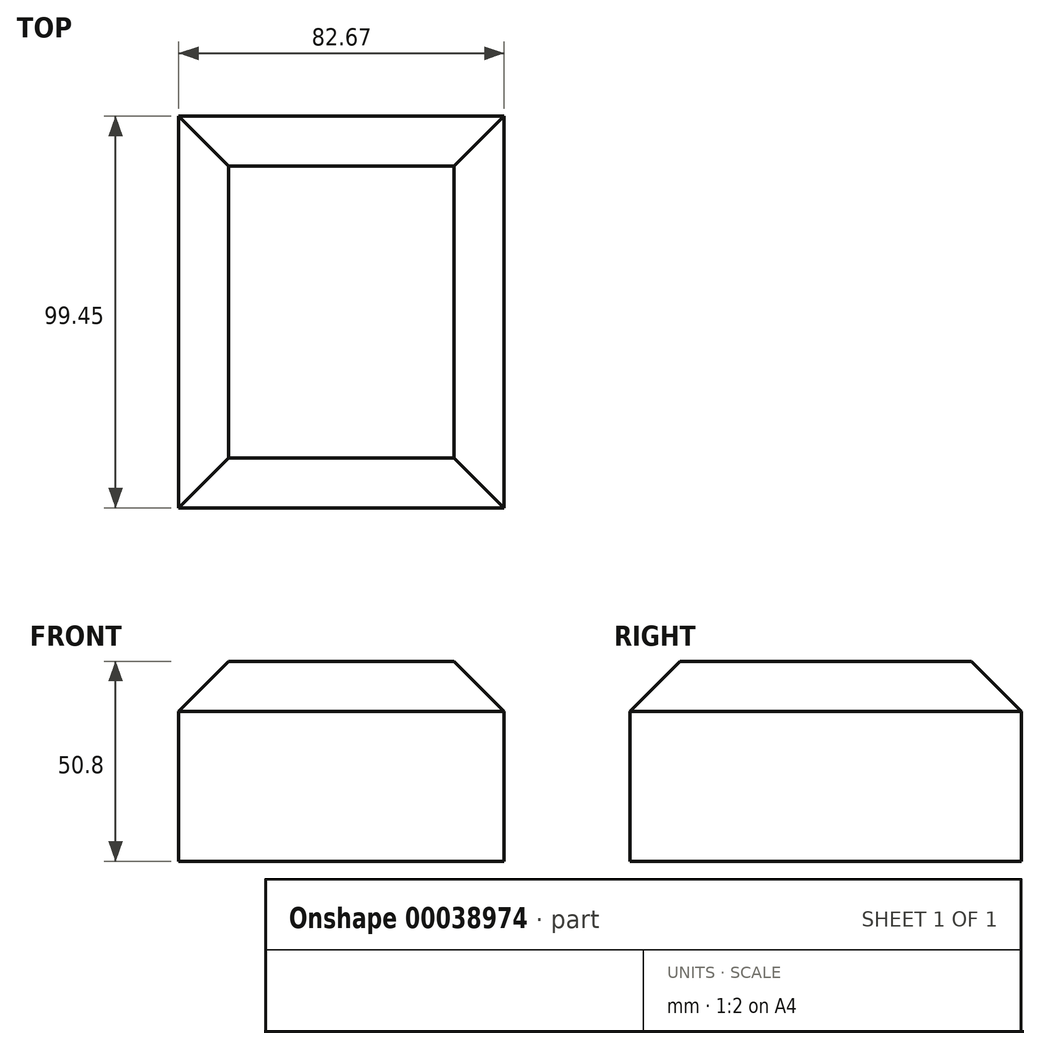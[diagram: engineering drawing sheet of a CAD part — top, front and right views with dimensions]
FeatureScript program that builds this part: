
annotation { "Feature Type Name" : "Feature", "Feature Type Description" : "" }
export const myFeature = defineFeature(function(context is Context, id is Id, definition is map)
    precondition{}
    {
        {
            var Q0;
            Q0=qCreatedBy(makeId("Top.planeOp"),FACE);
            var sketch = newSketch(context, id + "F0", { "sketchPlane" : qUnion([Q0])});
            skLineSegment(sketch, "E0.bottom", {"start": v(-82.67, -48.65) * mm, "end": v(0, -48.65) * mm});
            skLineSegment(sketch, "E0.top", {"start": v(-82.67, 50.8) * mm, "end": v(0, 50.8) * mm});
            skLineSegment(sketch, "E0.left", {"start": v(-82.67, -48.65) * mm, "end": v(-82.67, 50.8) * mm});
            skLineSegment(sketch, "E0.right", {"start": v(0, -48.65) * mm, "end": v(0, 50.8) * mm});
            skLineSegment(sketch, "E1.bottom", {"start": v(-82.67, 50.8) * mm, "end": v(-71.84, 50.8) * mm});
            skLineSegment(sketch, "E1.left", {"start": v(-82.67, 50.8) * mm, "end": v(-82.67, 0) * mm});
            skSolve(sketch);
        }
        {
            var Q0;
            Q0=makeQuery(id+"F0.imprint","IMPRINT",FACE,{"disambiguationData":[TD([[makeQuery(id+"F0.imprint","IMPRINT",EDGE,{"derivedFrom":sQuery(id+"F0.wireOp",EDGE,"E0.bottom")}),1.0]])]});
            extrude(context, id + "F1", {"entities" : qUnion([Q0]), "depth" : 50.8 * mm});
        }
        {
            var Q0;
            Q0=makeQuery(id+"F1.opExtrude","CAP_EDGE",EDGE,{"disambiguationData":[OSD([sQuery(id+"F0.wireOp",EDGE,"E0.bottom")])],"isStart":false});
            var Q1;
            Q1=makeQuery(id+"F1.opExtrude","CAP_EDGE",EDGE,{"disambiguationData":[OSD([sQuery(id+"F0.wireOp",EDGE,"E0.left"),sQuery(id+"F0.wireOp",EDGE,"E1.left")])],"isStart":false});
            var Q2;
            Q2=makeQuery(id+"F1.opExtrude","CAP_EDGE",EDGE,{"disambiguationData":[OSD([sQuery(id+"F0.wireOp",EDGE,"E0.right")])],"isStart":false});
            var Q3;
            Q3=makeQuery(id+"F1.opExtrude","CAP_EDGE",EDGE,{"disambiguationData":[OSD([sQuery(id+"F0.wireOp",EDGE,"E0.top"),sQuery(id+"F0.wireOp",EDGE,"E1.bottom")])],"isStart":false});
            chamfer(context, id + "F2", {"entities" : qUnion([Q0, Q1, Q2, Q3]), "width" : 12.7 * mm, "tangentPropagation" : true});
        }
    });
